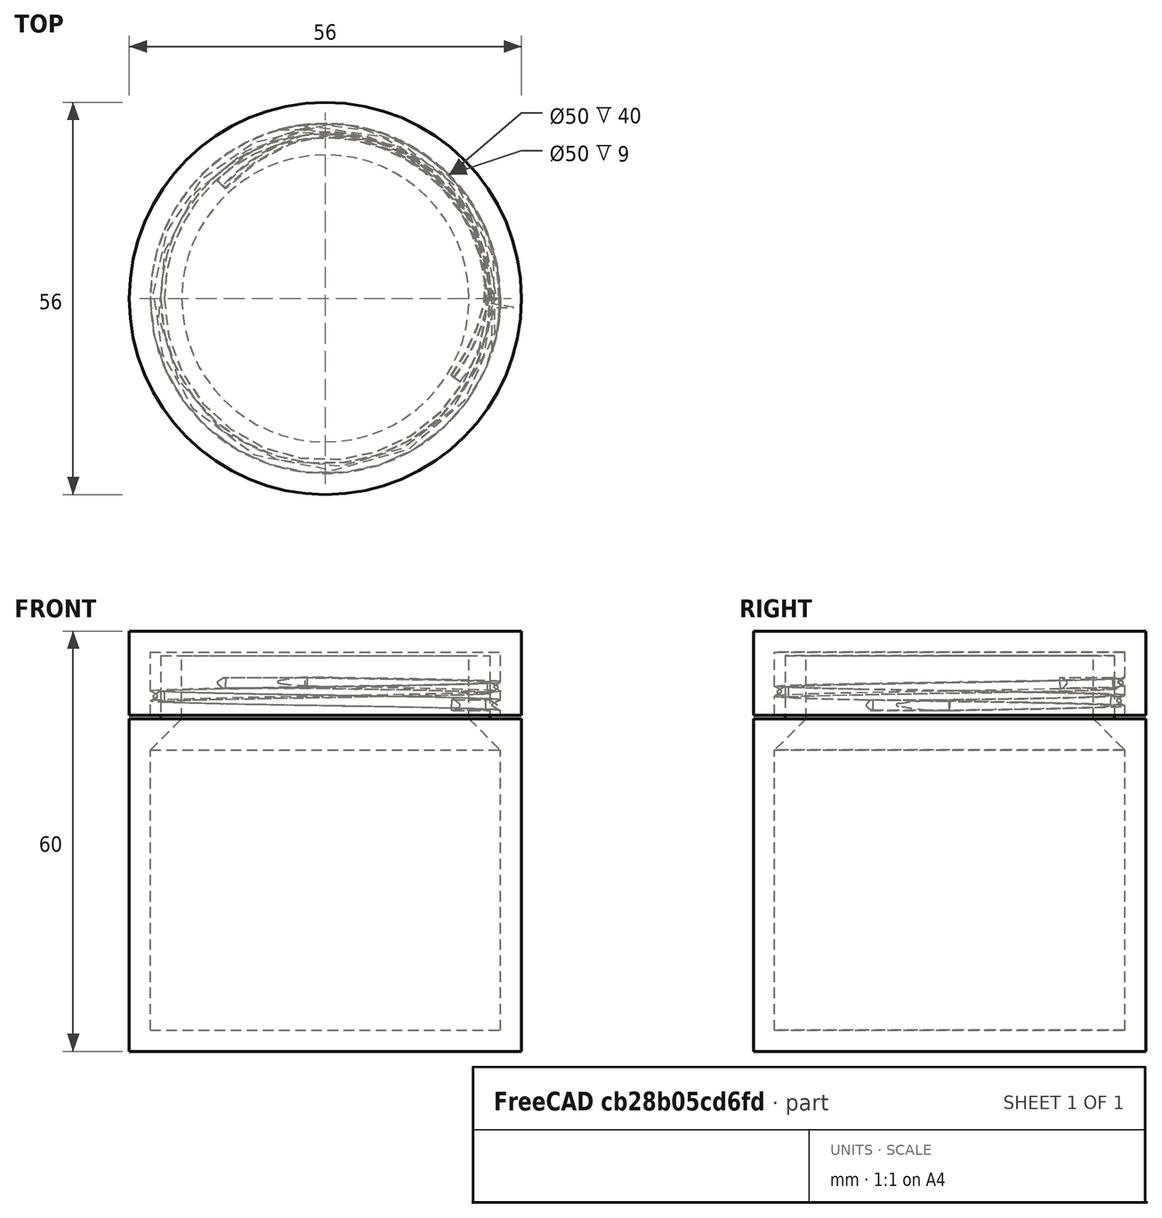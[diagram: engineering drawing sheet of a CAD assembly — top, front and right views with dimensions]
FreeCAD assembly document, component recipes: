
FREECAD ASSEMBLY — COMPONENT RECIPES ("part41-screw_top_container")

This assembly document has 2 components, labeled P0..P1 below (a component is one placed body or linked part). 0 of them carry a construction recipe — the FreeCAD feature program that regenerates the part from scratch, quoted from this document or its linked companion documents; the rest are supplied as boundary geometry only. No exploded tour is included for this assembly.
COMPONENT P0 — geometry summary ("Fusion002"; no construction recipe available for this part):
  bounding box: 56.4 x 56.0 x 13.8 mm
  tessellated surface: 45,156 triangles
  volume: 12062 mm^3 (28% of its bounding box)
COMPONENT P1 — geometry summary ("Fusion003"; no construction recipe available for this part):
  bounding box: 56.5 x 56.0 x 56.0 mm
  tessellated surface: 55,962 triangles
  volume: 35197 mm^3 (20% of its bounding box)
  symmetry: revolution-symmetric about the z axis through its bounding-box center; mirror-symmetric across its x mid-plane, y mid-plane
PROVENANCE & LICENSES
A FreeCAD (.FCStd) document from a public repository crawl; recipes are the document's own serialized feature recipes (and, for linked parts, companion documents' recipes).
License: as declared in the source repository (recorded in the dataset sidecar).
